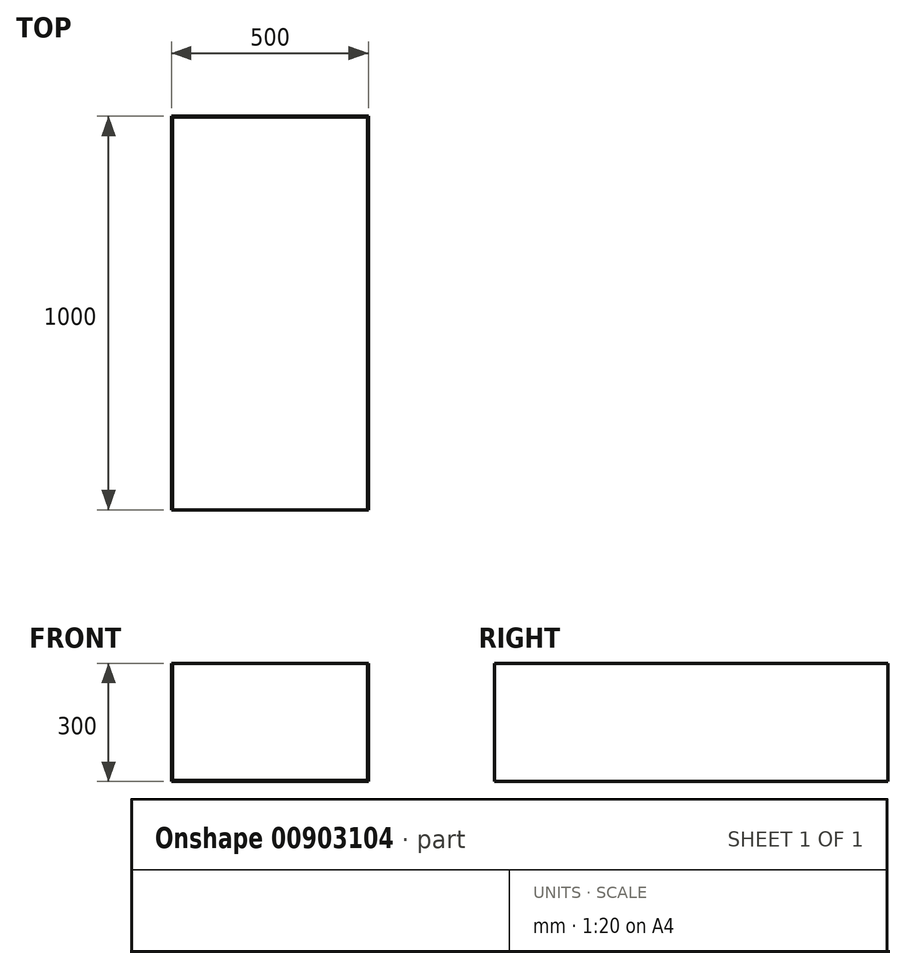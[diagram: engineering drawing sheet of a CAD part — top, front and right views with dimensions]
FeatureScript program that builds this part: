
annotation { "Feature Type Name" : "Feature", "Feature Type Description" : "" }
export const myFeature = defineFeature(function(context is Context, id is Id, definition is map)
    precondition{}
    {
        {
            var Q0;
            Q0=qCreatedBy(makeId("Front.planeOp"),FACE);
            var sketch = newSketch(context, id + "F0", { "sketchPlane" : qUnion([Q0])});
            skLineSegment(sketch, "E0.bottom", {"start": v(-335.73, 152.16) * mm, "end": v(164.27, 152.16) * mm});
            skLineSegment(sketch, "E0.top", {"start": v(-335.73, -147.84) * mm, "end": v(164.27, -147.84) * mm});
            skLineSegment(sketch, "E0.left", {"start": v(-335.73, 152.16) * mm, "end": v(-335.73, -147.84) * mm});
            skLineSegment(sketch, "E0.right", {"start": v(164.27, 152.16) * mm, "end": v(164.27, -147.84) * mm});
            skSolve(sketch);
        }
        {
            var Q0;
            Q0=makeQuery(id+"F0.imprint","IMPRINT",FACE,{"disambiguationData":[TD([[makeQuery(id+"F0.imprint","IMPRINT",EDGE,{"derivedFrom":sQuery(id+"F0.wireOp",EDGE,"E0.bottom")}),-1.0]])]});
            extrude(context, id + "F1", {"entities" : qUnion([Q0]), "depth" : 1000 * mm, "offsetDistance" : 25 * mm});
        }
        {
            var Q0;
            Q0=makeQuery(id+"F1.opExtrude","SWEPT_FACE",FACE,{"disambiguationData":[OSD([sQuery(id+"F0.wireOp",EDGE,"E0.bottom")])]});
            var Q1;
            Q1=makeQuery(id+"F1.opExtrude","CAP_FACE",FACE,{"disambiguationData":[OSD([sQuery(id+"F0.wireOp",EDGE,"E0.bottom"),sQuery(id+"F0.wireOp",EDGE,"E0.top"),sQuery(id+"F0.wireOp",EDGE,"E0.left"),sQuery(id+"F0.wireOp",EDGE,"E0.right")])],"isStart":false});
            shell(context, id + "F2", {"entities" : qUnion([Q0, Q1]), "thickness" : 2.5 * mm});
        }
    });
